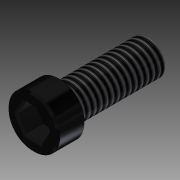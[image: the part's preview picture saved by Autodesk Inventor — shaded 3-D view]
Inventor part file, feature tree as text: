
AUTODESK INVENTOR PART (.ipt)
format: ipt  version: 2013 (Build 170138000, 138)  size: 114,688 bytes
history: native  units: in
note: dims shown in document units (in); Inventor stores cm internally (conversion verified against a paired STEP export)
features: extrude x3, sketch x1, thread x1, chamfer x1
ambient origin geometry x8: Origin, YZ Plane, XZ Plane, XY Plane, X Axis, Y Axis, Z Axis, Center Point
bodies: Solid1 (feature_tree)
feature tree (6):
  sketch  "Sketch1"  dims[d0=0.275in d1=0.185in d2=0.15in d3=0.15in d4=0.0in d5=0.465in d6=0.0in d7=0.05in d8=0.0in d9=1.0in d10=0.0in d11=0.01in d12=0.125in d13=45.0deg]
  extrude  "Extrusion1"  Depth=0.185in
  extrude  "Extrusion2"  Depth=0.15in
  extrude  "Extrusion3"  Depth=0.15in TaperAngle=0.0deg
  thread  "Thread1"  [1 undecoded]
  chamfer  "Chamfer1"  Distance=0.05in
note: 1 required parameter value undecoded (feature->parameter linkage not recoverable at this tier; creation-order binding heuristic only, values carry confidence <= 0.55)
